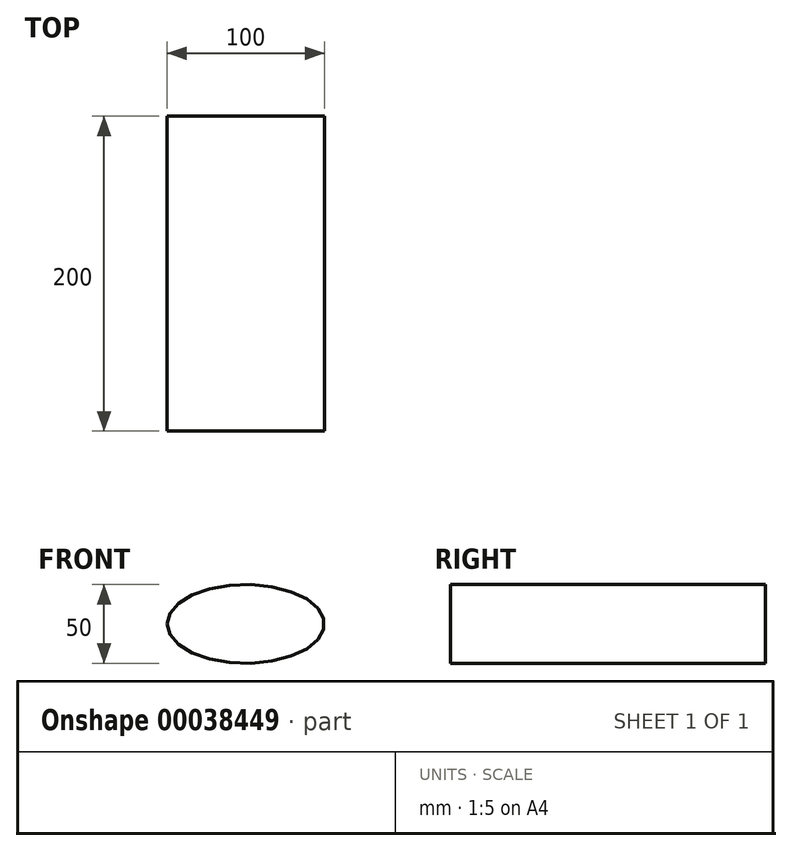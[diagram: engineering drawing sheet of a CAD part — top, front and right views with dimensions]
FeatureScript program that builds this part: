
annotation { "Feature Type Name" : "Feature", "Feature Type Description" : "" }
export const myFeature = defineFeature(function(context is Context, id is Id, definition is map)
    precondition{}
    {
        {
            var Q0;
            Q0=qCreatedBy(makeId("Front.planeOp"),FACE);
            var sketch = newSketch(context, id + "F0", { "sketchPlane" : qUnion([Q0])});
            skEllipse(sketch, "E0", {"center": v(0, 0) * mm, "majorRadius": 50 * mm, "minorRadius": 25 * mm, "majorAxis": v(-1, 0)});
            skSolve(sketch);
        }
        {
            var Q0;
            Q0=makeQuery(id+"F0.imprint","IMPRINT",FACE,{"disambiguationData":[TD([[makeQuery(id+"F0.imprint","IMPRINT",EDGE,{"derivedFrom":sQuery(id+"F0.wireOp",EDGE,"E0")}),1.0]])]});
            extrude(context, id + "F1", {"entities" : qUnion([Q0]), "depth" : 200 * mm});
        }
    });
